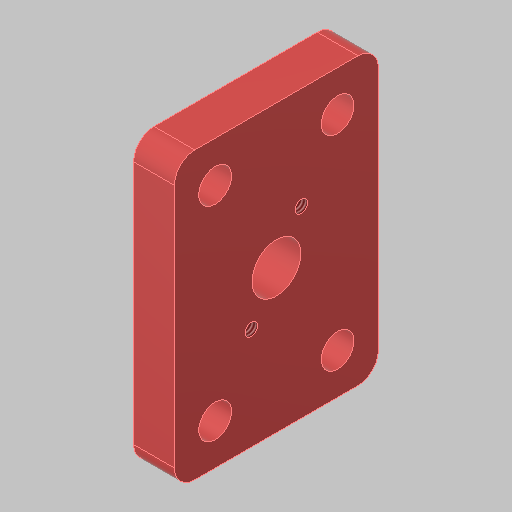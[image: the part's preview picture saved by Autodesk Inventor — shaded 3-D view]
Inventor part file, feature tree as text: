
AUTODESK INVENTOR PART (.ipt)
format: ipt  version: 2023.5 (Build 275446000, 446)  size: 137,216 bytes
history: native  units: in
note: dims shown in document units (in); Inventor stores cm internally (conversion verified against a paired STEP export)
features: sketch x3, extrude x2, hole x2, fillet x1
ambient origin geometry x8: Origin, YZ Plane, XZ Plane, XY Plane, X Axis, Y Axis, Z Axis, Center Point
bodies: Solid1 (feature_tree)
feature tree (8):
  sketch  "Sketch1"  dims[d0=1.75in d1=1.25in]
  extrude  "Extrusion1"  Depth=1.25in
  hole  "Hole1"  [1 undecoded]
  hole  "Hole2"  [1 undecoded]
  extrude  "Extrusion2"  Depth=0.25in
  fillet  "Fillet1"  Radius=0.25in
  sketch  "Sketch2"  dims[d2=1.25in d3=0.75in]
  sketch  "Sketch3"  dims[d4=0.25in d5=0.0in d6=0.201in d7=0.38in d8=0.385in d9=0.25in d10=0.5635in d11=1.0in d12=0.8108in d13=0.586in d14=0.0764in d15=0.198in d16=0.375in d17=0.25in d18=0.5635in d19=1.0in d20=0.8108in d21=0.3in d22=0.25in d23=0.0in d24=0.125in d27=0.25in]
note: 2 required parameter values undecoded (feature->parameter linkage not recoverable at this tier; creation-order binding heuristic only, values carry confidence <= 0.55)
